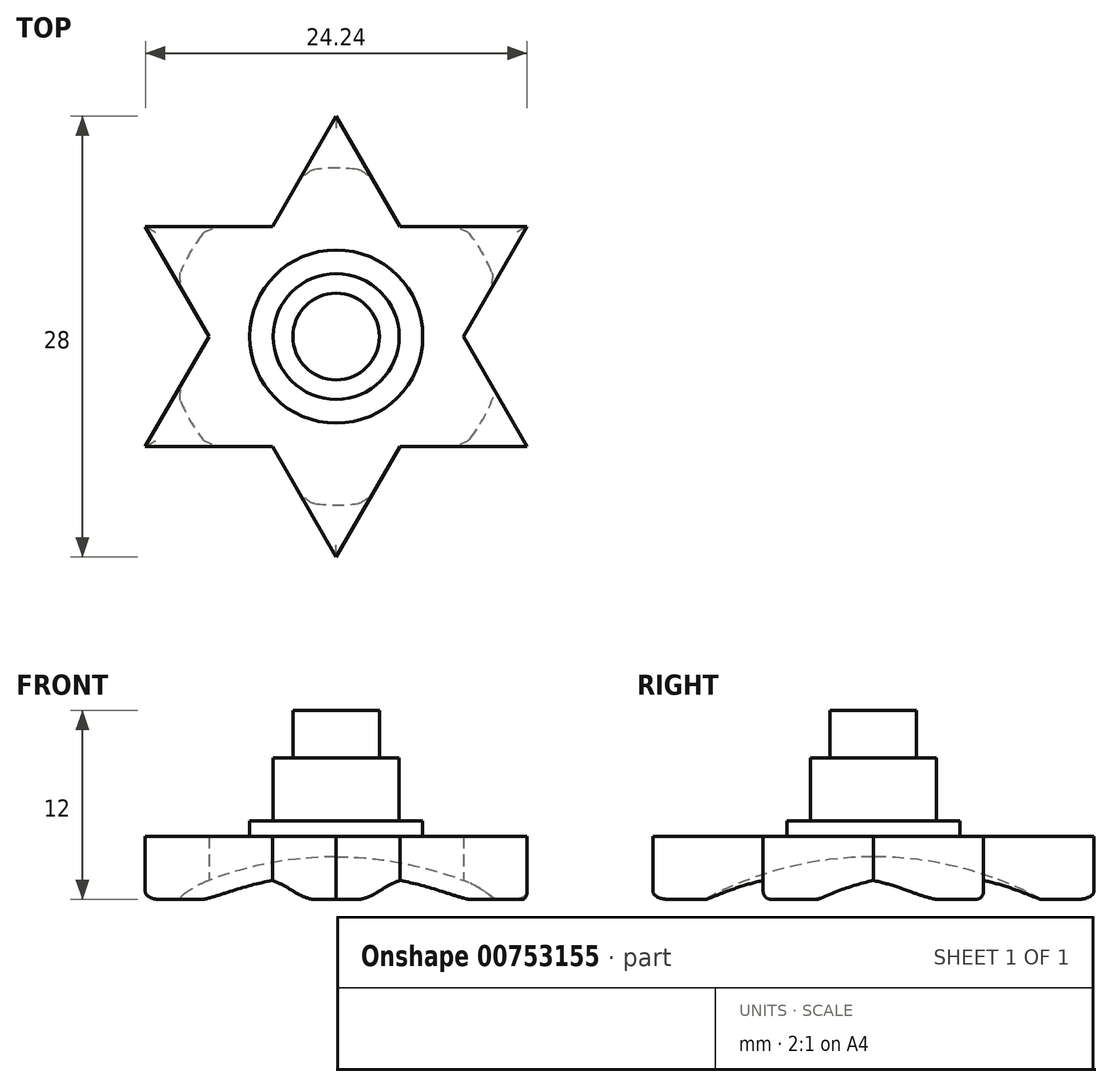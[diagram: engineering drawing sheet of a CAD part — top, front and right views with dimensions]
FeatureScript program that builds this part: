
annotation { "Feature Type Name" : "Feature", "Feature Type Description" : "" }
export const myFeature = defineFeature(function(context is Context, id is Id, definition is map)
    precondition{}
    {
        {
            var Q0;
            Q0=qCreatedBy(makeId("Top.planeOp"),FACE);
            var sketch = newSketch(context, id + "F0", { "sketchPlane" : qUnion([Q0])});
            skCircle(sketch, "E0", {"center": v(0, 0) * mm, "radius": 14 * mm, "construction": true});
            skLineSegment(sketch, "E1", {"start": v(-12.12, 7) * mm, "end": v(12.12, 7) * mm});
            skLineSegment(sketch, "E2", {"start": v(12.12, 7) * mm, "end": v(0, -14) * mm});
            skLineSegment(sketch, "E3", {"start": v(0, -14) * mm, "end": v(-12.12, 7) * mm});
            skLineSegment(sketch, "E4", {"start": v(-12.12, -7) * mm, "end": v(12.12, -7) * mm});
            skLineSegment(sketch, "E5", {"start": v(12.12, -7) * mm, "end": v(0, 14) * mm});
            skPoint(sketch, "E5.endSnap0", {"position": v(0, 7) * mm});
            skLineSegment(sketch, "E6", {"start": v(0, 14) * mm, "end": v(-12.12, -7) * mm});
            skSolve(sketch);
        }
        {
            var Q0;
            Q0=qSketchRegion(id+"F0",true);
            extrude(context, id + "F1", {"entities" : qUnion([Q0]), "flatOperationType" : FlatOperationType.REMOVE, "depth" : 4 * mm, "offsetDistance" : 25 * mm, "domain" : OperationDomain.MODEL});
        }
        {
            var Q0;
            Q0=qCreatedBy(makeId("Front.planeOp"),FACE);
            var sketch = newSketch(context, id + "F2", { "sketchPlane" : qUnion([Q0])});
            skLineSegment(sketch, "E7", {"start": v(0, 0) * mm, "end": v(0, -4.5) * mm, "construction": true});
            skSolve(sketch);
        }
        {
            var Q0;
            Q0=qCreatedBy(makeId("Front.planeOp"),FACE);
            var sketch = newSketch(context, id + "F3", { "sketchPlane" : qUnion([Q0])});
            skArc(sketch, "E8", {"start": v(0, 2.7) * mm, "mid": v(-22.55, -19.85) * mm, "end": v(0, -42.4) * mm});
            skLineSegment(sketch, "E9", {"start": v(0, 2.7) * mm, "end": v(0, -42.4) * mm});
            skPoint(sketch, "E10", {"position": v(-10.7, 0) * mm});
            skSolve(sketch);
        }
        {
            var Q0;
            Q0=qSketchRegion(id+"F3",true);
            var Q1;
            Q1=sQuery(id+"F3.wireOp",EDGE,"E9");
            revolve(context, id + "F4", {"operationType" : NewBodyOperationType.REMOVE, "surfaceOperationType" : NewSurfaceOperationType.NEW, "entities" : qUnion([Q0]), "axis" : qUnion([Q1]), "revolveType" : RevolveType.FULL, "oppositeDirection" : true});
        }
        {
            var Q0;
            Q0=makeQuery(id+"F1.opExtrude","CAP_FACE",FACE,{"disambiguationData":[OSD([sQuery(id+"F0.wireOp",EDGE,"E1"),sQuery(id+"F0.wireOp",EDGE,"E2"),sQuery(id+"F0.wireOp",EDGE,"E3"),sQuery(id+"F0.wireOp",EDGE,"E4"),sQuery(id+"F0.wireOp",EDGE,"E5"),sQuery(id+"F0.wireOp",EDGE,"E6")])],"isStart":false});
            var sketch = newSketch(context, id + "F5", { "sketchPlane" : qUnion([Q0])});
            skCircle(sketch, "E11", {"center": v(0, 0) * mm, "radius": 5.5 * mm});
            skSolve(sketch);
        }
        {
            var Q0;
            Q0=qSketchRegion(id+"F5",true);
            extrude(context, id + "F6", {"entities" : qUnion([Q0]), "operationType" : NewBodyOperationType.ADD, "flatOperationType" : FlatOperationType.REMOVE, "depth" : 1 * mm, "offsetDistance" : 25 * mm, "domain" : OperationDomain.MODEL});
        }
        {
            var Q0;
            Q0=makeQuery(id+"F6.opExtrude","CAP_FACE",FACE,{"disambiguationData":[OSD([sQuery(id+"F5.wireOp",EDGE,"E11")])],"isStart":false});
            var sketch = newSketch(context, id + "F7", { "sketchPlane" : qUnion([Q0])});
            skCircle(sketch, "E12", {"center": v(0, 0) * mm, "radius": 4 * mm});
            skSolve(sketch);
        }
        {
            var Q0;
            Q0=qSketchRegion(id+"F7",true);
            extrude(context, id + "F8", {"entities" : qUnion([Q0]), "operationType" : NewBodyOperationType.ADD, "depth" : 4 * mm, "offsetDistance" : 25 * mm});
        }
        {
            var Q0;
            Q0=makeQuery(id+"F8.opExtrude","CAP_FACE",FACE,{"disambiguationData":[OSD([sQuery(id+"F7.wireOp",EDGE,"E12")])],"isStart":false});
            var sketch = newSketch(context, id + "F9", { "sketchPlane" : qUnion([Q0])});
            skCircle(sketch, "E13", {"center": v(0, 0) * mm, "radius": 2.75 * mm});
            skSolve(sketch);
        }
        {
            var Q0;
            Q0=qSketchRegion(id+"F9",true);
            extrude(context, id + "F10", {"entities" : qUnion([Q0]), "operationType" : NewBodyOperationType.ADD, "flatOperationType" : FlatOperationType.REMOVE, "depth" : 3 * mm, "offsetDistance" : 25 * mm, "domain" : OperationDomain.MODEL});
        }
        {
            var Q0;
            Q0=makeQuery(id+"F1.opExtrude","CAP_EDGE",EDGE,{"disambiguationData":[OSD([sQuery(id+"F0.wireOp",EDGE,"1e846c76-ade1-459f-9f20-eea542154bc1.trimOffspring")])],"isStart":true});
            var Q1;
            Q1=makeQuery(id+"F4.boolean.opBoolean","INTERSECT",EDGE,{"disambiguationData":[OD(0.0)],"derivedFrom":[makeQuery(id+"F1.opExtrude","SWEPT_FACE",FACE,{"disambiguationData":[OSD([sQuery(id+"F0.wireOp",EDGE,"1e846c76-ade1-459f-9f20-eea542154bc1.trimOffspring")])]}),makeQuery(id+"F4.opRevolve","SWEPT_FACE",FACE,{"disambiguationData":[OSD([sQuery(id+"F3.wireOp",EDGE,"E8")])]})]});
            var Q2;
            Q2=makeQuery(id+"F4.boolean.opBoolean","INTERSECT",EDGE,{"disambiguationData":[OD(1.0)],"derivedFrom":[makeQuery(id+"F1.opExtrude","SWEPT_FACE",FACE,{"disambiguationData":[OSD([sQuery(id+"F0.wireOp",EDGE,"1e846c76-ade1-459f-9f20-eea542154bc1.trimOffspring")])]}),makeQuery(id+"F4.opRevolve","SWEPT_FACE",FACE,{"disambiguationData":[OSD([sQuery(id+"F3.wireOp",EDGE,"E8")])]})]});
            var Q3;
            Q3=makeQuery(id+"F4.boolean.opBoolean","INTERSECT",EDGE,{"disambiguationData":[OD(1.0)],"derivedFrom":[makeQuery(id+"F1.opExtrude","SWEPT_FACE",FACE,{"disambiguationData":[OSD([sQuery(id+"F0.wireOp",EDGE,"tKFEvPMP-PRdD-FNsb-sHzV-FJ5KZ0vE21vF")])]}),makeQuery(id+"F4.opRevolve","SWEPT_FACE",FACE,{"disambiguationData":[OSD([sQuery(id+"F3.wireOp",EDGE,"E8")])]})]});
            var Q4;
            Q4=makeQuery(id+"F1.opExtrude","CAP_EDGE",EDGE,{"disambiguationData":[OSD([sQuery(id+"F0.wireOp",EDGE,"tKFEvPMP-PRdD-FNsb-sHzV-FJ5KZ0vE21vF")])],"isStart":true});
            var Q5;
            Q5=makeQuery(id+"F4.boolean.opBoolean","INTERSECT",EDGE,{"disambiguationData":[OD(0.0)],"derivedFrom":[makeQuery(id+"F1.opExtrude","SWEPT_FACE",FACE,{"disambiguationData":[OSD([sQuery(id+"F0.wireOp",EDGE,"tKFEvPMP-PRdD-FNsb-sHzV-FJ5KZ0vE21vF")])]}),makeQuery(id+"F4.opRevolve","SWEPT_FACE",FACE,{"disambiguationData":[OSD([sQuery(id+"F3.wireOp",EDGE,"E8")])]})]});
            var Q6;
            Q6=makeQuery(id+"F4.boolean.opBoolean","INTERSECT",EDGE,{"derivedFrom":[makeQuery(id+"F1.opExtrude","SWEPT_FACE",FACE,{"disambiguationData":[OSD([sQuery(id+"F0.wireOp",EDGE,"242ec415-8ae3-4f29-b666-454949ffb425")])]}),makeQuery(id+"F4.opRevolve","SWEPT_FACE",FACE,{"disambiguationData":[OSD([sQuery(id+"F3.wireOp",EDGE,"E8")])]})]});
            var Q7;
            Q7=makeQuery(id+"F4.boolean.opBoolean","INTERSECT",EDGE,{"derivedFrom":[makeQuery(id+"F1.opExtrude","SWEPT_FACE",FACE,{"disambiguationData":[OSD([sQuery(id+"F0.wireOp",EDGE,"2e8c3351-43db-4b2f-8d93-3145ab630699")])]}),makeQuery(id+"F4.opRevolve","SWEPT_FACE",FACE,{"disambiguationData":[OSD([sQuery(id+"F3.wireOp",EDGE,"E8")])]})]});
            var Q8;
            Q8=makeQuery(id+"F4.boolean.opBoolean","INTERSECT",EDGE,{"derivedFrom":[makeQuery(id+"F1.opExtrude","SWEPT_FACE",FACE,{"disambiguationData":[OSD([sQuery(id+"F0.wireOp",EDGE,"0d916ec6-ba67-41f7-baff-9ab997f34d730.MirrorCS")])]}),makeQuery(id+"F4.opRevolve","SWEPT_FACE",FACE,{"disambiguationData":[OSD([sQuery(id+"F3.wireOp",EDGE,"E8")])]})]});
            var Q9;
            Q9=makeQuery(id+"F4.boolean.opBoolean","INTERSECT",EDGE,{"derivedFrom":[makeQuery(id+"F1.opExtrude","SWEPT_FACE",FACE,{"disambiguationData":[OSD([sQuery(id+"F0.wireOp",EDGE,"a457c902-26b3-4f10-bb78-2ab6ae07cb150.MirrorCS")])]}),makeQuery(id+"F4.opRevolve","SWEPT_FACE",FACE,{"disambiguationData":[OSD([sQuery(id+"F3.wireOp",EDGE,"E8")])]})]});
            var Q10;
            Q10=makeQuery(id+"F4.boolean.opBoolean","INTERSECT",EDGE,{"derivedFrom":[makeQuery(id+"F1.opExtrude","SWEPT_FACE",FACE,{"disambiguationData":[OSD([sQuery(id+"F0.wireOp",EDGE,"c5a32763-f214-434a-a679-c62fad5373420.MirrorCS")])]}),makeQuery(id+"F4.opRevolve","SWEPT_FACE",FACE,{"disambiguationData":[OSD([sQuery(id+"F3.wireOp",EDGE,"E8")])]})]});
            var Q11;
            Q11=makeQuery(id+"F4.boolean.opBoolean","INTERSECT",EDGE,{"derivedFrom":[makeQuery(id+"F1.opExtrude","SWEPT_FACE",FACE,{"disambiguationData":[OSD([sQuery(id+"F0.wireOp",EDGE,"3e29270c-300e-4125-b294-69302c5c2de7")])]}),makeQuery(id+"F4.opRevolve","SWEPT_FACE",FACE,{"disambiguationData":[OSD([sQuery(id+"F3.wireOp",EDGE,"E8")])]})]});
            var Q12;
            Q12=makeQuery(id+"F4.boolean.opBoolean","INTERSECT",EDGE,{"derivedFrom":[makeQuery(id+"F1.opExtrude","SWEPT_FACE",FACE,{"disambiguationData":[OSD([sQuery(id+"F0.wireOp",EDGE,"4566d7b5-300b-411e-9199-16c91fdfb8010.MirrorCS")])]}),makeQuery(id+"F4.opRevolve","SWEPT_FACE",FACE,{"disambiguationData":[OSD([sQuery(id+"F3.wireOp",EDGE,"E8")])]})]});
            var Q13;
            {var subQ0=sQuery(id+"F0.wireOp",EDGE,"E6");Q13=makeQuery(id+"F1.opExtrude","CAP_EDGE",EDGE,{"disambiguationData":[OSD([subQ0]),TDD([makeQuery(id+"F0.imprint","IMPRINT",EDGE,{"disambiguationData":[TD([[makeQuery(id+"F0.imprint","INTERSECT",VERTEX,{"derivedFrom":[sQuery(id+"F0.wireOp",EDGE,"E4"),subQ0]}),1.0]])],"derivedFrom":subQ0})])],"isStart":true});}
            var Q14;
            {var subQ0=sQuery(id+"F0.wireOp",EDGE,"E3");Q14=makeQuery(id+"F1.opExtrude","CAP_EDGE",EDGE,{"disambiguationData":[OSD([subQ0]),TDD([makeQuery(id+"F0.imprint","IMPRINT",EDGE,{"disambiguationData":[TD([[makeQuery(id+"F0.imprint","INTERSECT",VERTEX,{"derivedFrom":[sQuery(id+"F0.wireOp",EDGE,"E1"),subQ0]}),1.0]])],"derivedFrom":subQ0})])],"isStart":true});}
            var Q15;
            {var subQ0=sQuery(id+"F0.wireOp",EDGE,"E6");Q15=makeQuery(id+"F1.opExtrude","CAP_EDGE",EDGE,{"disambiguationData":[OSD([subQ0]),TDD([makeQuery(id+"F0.imprint","IMPRINT",EDGE,{"disambiguationData":[TD([[makeQuery(id+"F0.imprint","INTERSECT",VERTEX,{"derivedFrom":[sQuery(id+"F0.wireOp",EDGE,"E5"),subQ0]}),-1.0]])],"derivedFrom":subQ0})])],"isStart":true});}
            var Q16;
            {var subQ0=sQuery(id+"F0.wireOp",EDGE,"E1");Q16=makeQuery(id+"F1.opExtrude","CAP_EDGE",EDGE,{"disambiguationData":[OSD([subQ0]),TDD([makeQuery(id+"F0.imprint","IMPRINT",EDGE,{"disambiguationData":[TD([[makeQuery(id+"F0.imprint","INTERSECT",VERTEX,{"derivedFrom":[subQ0,sQuery(id+"F0.wireOp",EDGE,"E3")]}),-1.0]])],"derivedFrom":subQ0})])],"isStart":true});}
            var Q17;
            {var subQ0=sQuery(id+"F0.wireOp",EDGE,"E1");Q17=makeQuery(id+"F1.opExtrude","CAP_EDGE",EDGE,{"disambiguationData":[OSD([subQ0]),TDD([makeQuery(id+"F0.imprint","IMPRINT",EDGE,{"disambiguationData":[TD([[makeQuery(id+"F0.imprint","INTERSECT",VERTEX,{"derivedFrom":[subQ0,sQuery(id+"F0.wireOp",EDGE,"E2")]}),1.0]])],"derivedFrom":subQ0})])],"isStart":true});}
            var Q18;
            {var subQ0=sQuery(id+"F0.wireOp",EDGE,"E3");Q18=makeQuery(id+"F1.opExtrude","CAP_EDGE",EDGE,{"disambiguationData":[OSD([subQ0]),TDD([makeQuery(id+"F0.imprint","IMPRINT",EDGE,{"disambiguationData":[TD([[makeQuery(id+"F0.imprint","INTERSECT",VERTEX,{"derivedFrom":[sQuery(id+"F0.wireOp",EDGE,"E2"),subQ0]}),-1.0]])],"derivedFrom":subQ0})])],"isStart":true});}
            var Q19;
            {var subQ0=sQuery(id+"F0.wireOp",EDGE,"E5");Q19=makeQuery(id+"F1.opExtrude","CAP_EDGE",EDGE,{"disambiguationData":[OSD([subQ0]),TDD([makeQuery(id+"F0.imprint","IMPRINT",EDGE,{"disambiguationData":[TD([[makeQuery(id+"F0.imprint","INTERSECT",VERTEX,{"derivedFrom":[subQ0,sQuery(id+"F0.wireOp",EDGE,"E6")]}),1.0]])],"derivedFrom":subQ0})])],"isStart":true});}
            var Q20;
            {var subQ0=sQuery(id+"F0.wireOp",EDGE,"E4");Q20=makeQuery(id+"F1.opExtrude","CAP_EDGE",EDGE,{"disambiguationData":[OSD([subQ0]),TDD([makeQuery(id+"F0.imprint","IMPRINT",EDGE,{"disambiguationData":[TD([[makeQuery(id+"F0.imprint","INTERSECT",VERTEX,{"derivedFrom":[subQ0,sQuery(id+"F0.wireOp",EDGE,"E6")]}),-1.0]])],"derivedFrom":subQ0})])],"isStart":true});}
            var Q21;
            {var subQ0=sQuery(id+"F0.wireOp",EDGE,"E2");Q21=makeQuery(id+"F1.opExtrude","CAP_EDGE",EDGE,{"disambiguationData":[OSD([subQ0]),TDD([makeQuery(id+"F0.imprint","IMPRINT",EDGE,{"disambiguationData":[TD([[makeQuery(id+"F0.imprint","INTERSECT",VERTEX,{"derivedFrom":[subQ0,sQuery(id+"F0.wireOp",EDGE,"E3")]}),1.0]])],"derivedFrom":subQ0})])],"isStart":true});}
            var Q22;
            {var subQ0=sQuery(id+"F0.wireOp",EDGE,"E4");Q22=makeQuery(id+"F1.opExtrude","CAP_EDGE",EDGE,{"disambiguationData":[OSD([subQ0]),TDD([makeQuery(id+"F0.imprint","IMPRINT",EDGE,{"disambiguationData":[TD([[makeQuery(id+"F0.imprint","INTERSECT",VERTEX,{"derivedFrom":[subQ0,sQuery(id+"F0.wireOp",EDGE,"E5")]}),1.0]])],"derivedFrom":subQ0})])],"isStart":true});}
            var Q23;
            {var subQ0=sQuery(id+"F0.wireOp",EDGE,"E2");Q23=makeQuery(id+"F1.opExtrude","CAP_EDGE",EDGE,{"disambiguationData":[OSD([subQ0]),TDD([makeQuery(id+"F0.imprint","IMPRINT",EDGE,{"disambiguationData":[TD([[makeQuery(id+"F0.imprint","INTERSECT",VERTEX,{"derivedFrom":[sQuery(id+"F0.wireOp",EDGE,"E1"),subQ0]}),-1.0]])],"derivedFrom":subQ0})])],"isStart":true});}
            fillet(context, id + "F11", {"entities" : qUnion([Q0, Q1, Q2, Q3, Q4, Q5, Q6, Q7, Q8, Q9, Q10, Q11, Q12, Q13, Q14, Q15, Q16, Q17, Q18, Q19, Q20, Q21, Q22, Q23]), "radius" : 0.5 * mm, "tangentPropagation" : true, "allowEdgeOverflow" : false});
        }
    });
